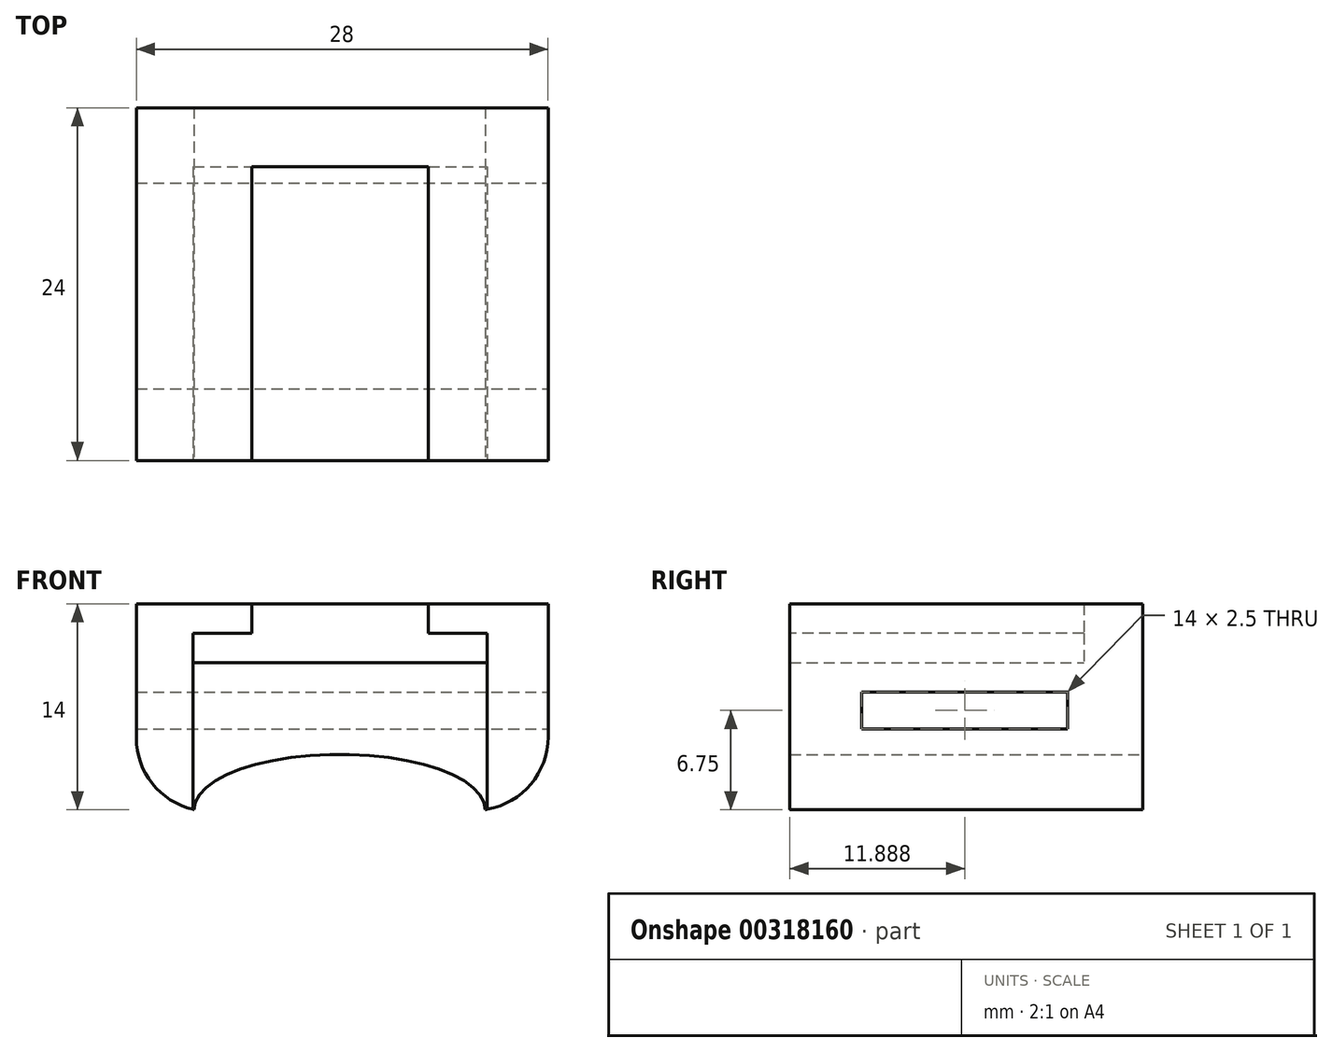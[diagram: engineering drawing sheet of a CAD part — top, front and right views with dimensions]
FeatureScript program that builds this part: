
annotation { "Feature Type Name" : "Feature", "Feature Type Description" : "" }
export const myFeature = defineFeature(function(context is Context, id is Id, definition is map)
    precondition{}
    {
        {
            var Q0;
            Q0=qCreatedBy(makeId("Top.planeOp"),FACE);
            var sketch = newSketch(context, id + "F0", { "sketchPlane" : qUnion([Q0])});
            skLineSegment(sketch, "E0.bottom", {"start": v(-9.96, 9.84) * mm, "end": v(10.04, 9.84) * mm});
            skLineSegment(sketch, "E0.top", {"start": v(-9.96, -10.16) * mm, "end": v(10.04, -10.16) * mm});
            skLineSegment(sketch, "E0.left", {"start": v(-9.96, 9.84) * mm, "end": v(-9.96, -10.16) * mm});
            skLineSegment(sketch, "E0.right", {"start": v(10.04, 9.84) * mm, "end": v(10.04, -10.16) * mm});
            skLineSegment(sketch, "E1.bottom", {"start": v(-13.83, 13.84) * mm, "end": v(14.17, 13.84) * mm});
            skLineSegment(sketch, "E1.top", {"start": v(-13.83, -10.16) * mm, "end": v(14.17, -10.16) * mm});
            skLineSegment(sketch, "E1.left", {"start": v(-13.83, 13.84) * mm, "end": v(-13.83, -10.16) * mm});
            skLineSegment(sketch, "E1.right", {"start": v(14.17, 13.84) * mm, "end": v(14.17, -10.16) * mm});
            skLineSegment(sketch, "E2", {"start": v(-5.96, 9.84) * mm, "end": v(-5.96, -10.16) * mm});
            skLineSegment(sketch, "E3", {"start": v(6.04, 9.84) * mm, "end": v(6.04, -10.16) * mm});
            skLineSegment(sketch, "E4.bottom", {"start": v(-35.1, 18.75) * mm, "end": v(34.9, 18.75) * mm});
            skLineSegment(sketch, "E4.top", {"start": v(-35.1, -15.3) * mm, "end": v(34.9, -15.3) * mm});
            skLineSegment(sketch, "E4.left", {"start": v(-35.1, 18.75) * mm, "end": v(-35.1, -15.3) * mm});
            skLineSegment(sketch, "E4.right", {"start": v(34.9, 18.75) * mm, "end": v(34.9, -15.3) * mm});
            skSolve(sketch);
        }
        {
            var Q0;
            {var subQ0=sQuery(id+"F0.wireOp",EDGE,"E0.left");Q0=makeQuery(id+"F0.imprint","IMPRINT",FACE,{"disambiguationData":[TD([[makeQuery(id+"F0.imprint","IMPRINT",EDGE,{"derivedFrom":subQ0}),1.0]])]});}
            var Q1;
            {var subQ1=sQuery(id+"F0.wireOp",EDGE,"E0.left");Q1=makeQuery(id+"F0.imprint","IMPRINT",FACE,{"disambiguationData":[TD([[makeQuery(id+"F0.imprint","IMPRINT",EDGE,{"derivedFrom":subQ1}),-1.0]])]});}
            var Q2;
            {var subQ0=sQuery(id+"F0.wireOp",EDGE,"E0.right");Q2=makeQuery(id+"F0.imprint","IMPRINT",FACE,{"disambiguationData":[TD([[makeQuery(id+"F0.imprint","IMPRINT",EDGE,{"derivedFrom":subQ0}),-1.0]])]});}
            var Q3;
            {var subQ0=sQuery(id+"F0.wireOp",EDGE,"E2");Q3=makeQuery(id+"F0.imprint","IMPRINT",FACE,{"disambiguationData":[TD([[makeQuery(id+"F0.imprint","IMPRINT",EDGE,{"derivedFrom":subQ0}),1.0]])]});}
            extrude(context, id + "F1", {"entities" : qUnion([Q0, Q1, Q2, Q3]), "depth" : 10 * mm, "offsetDistance" : 25 * mm});
        }
        {
            var Q0;
            {var subQ1=sQuery(id+"F0.wireOp",EDGE,"E0.left");Q0=makeQuery(id+"F0.imprint","IMPRINT",FACE,{"disambiguationData":[TD([[makeQuery(id+"F0.imprint","IMPRINT",EDGE,{"derivedFrom":subQ1}),-1.0]])]});}
            extrude(context, id + "F2", {"entities" : qUnion([Q0]), "operationType" : NewBodyOperationType.ADD, "depth" : 14 * mm, "offsetDistance" : 25 * mm});
        }
        {
            var Q0;
            {var subQ0=sQuery(id+"F0.wireOp",EDGE,"E0.right");var subQ1=sQuery(id+"F0.wireOp",EDGE,"E0.bottom");var subQ2=makeQuery(id+"F0.imprint","INTERSECT",VERTEX,{"derivedFrom":[subQ1,subQ0]});Q0=makeQuery(id+"F0.imprint","IMPRINT",FACE,{"disambiguationData":[TD([[makeQuery(id+"F0.imprint","IMPRINT",EDGE,{"disambiguationData":[TD([[subQ2,1.0]])],"derivedFrom":subQ1}),-1.0]])]});}
            var Q1;
            {var subQ0=sQuery(id+"F0.wireOp",EDGE,"E0.left");var subQ1=sQuery(id+"F0.wireOp",EDGE,"E0.bottom");var subQ2=makeQuery(id+"F0.imprint","INTERSECT",VERTEX,{"derivedFrom":[subQ1,subQ0]});Q1=makeQuery(id+"F0.imprint","IMPRINT",FACE,{"disambiguationData":[TD([[makeQuery(id+"F0.imprint","IMPRINT",EDGE,{"disambiguationData":[TD([[subQ2,-1.0]])],"derivedFrom":subQ1}),-1.0]])]});}
            extrude(context, id + "F3", {"entities" : qUnion([Q0, Q1]), "operationType" : NewBodyOperationType.ADD, "depth" : 14 * mm, "offsetDistance" : 25 * mm, "hasSecondDirection" : true, "secondDirectionOppositeDirection" : false, "secondDirectionDepth" : 12 * mm});
        }
        {
            var Q0;
            Q0=qCreatedBy(makeId("Right.planeOp"),FACE);
            var sketch = newSketch(context, id + "F4", { "sketchPlane" : qUnion([Q0])});
            skLineSegment(sketch, "E5.bottom", {"start": v(8.73, 8) * mm, "end": v(-5.27, 8) * mm});
            skLineSegment(sketch, "E5.top", {"start": v(8.73, 5.5) * mm, "end": v(-5.27, 5.5) * mm});
            skLineSegment(sketch, "E5.left", {"start": v(8.73, 8) * mm, "end": v(8.73, 5.5) * mm});
            skLineSegment(sketch, "E5.right", {"start": v(-5.27, 8) * mm, "end": v(-5.27, 5.5) * mm});
            skSolve(sketch);
        }
        {
            var Q0;
            Q0=makeQuery(id+"F4.imprint","IMPRINT",FACE,{"disambiguationData":[TD([[makeQuery(id+"F4.imprint","IMPRINT",EDGE,{"derivedFrom":sQuery(id+"F4.wireOp",EDGE,"E5.bottom")}),1.0]])]});
            extrude(context, id + "F5", {"entities" : qUnion([Q0]), "operationType" : NewBodyOperationType.REMOVE, "oppositeDirection" : true, "depth" : 25 * mm, "offsetDistance" : 25 * mm, "hasSecondDirection" : true, "secondDirectionOppositeDirection" : false, "secondDirectionDepth" : 25 * mm});
        }
        {
            var Q0;
            Q0=qCreatedBy(makeId("Front.planeOp"),FACE);
            var sketch = newSketch(context, id + "F6", { "sketchPlane" : qUnion([Q0])});
            skEllipse(sketch, "E6", {"center": v(0, 0) * mm, "majorRadius": 9.9 * mm, "minorRadius": 3.76 * mm, "majorAxis": v(1, 0)});
            skSolve(sketch);
        }
        {
            var Q0;
            Q0=makeQuery(id+"F6.imprint","IMPRINT",FACE,{"disambiguationData":[TD([[makeQuery(id+"F6.imprint","IMPRINT",EDGE,{"derivedFrom":sQuery(id+"F6.wireOp",EDGE,"E6")}),1.0]])]});
            extrude(context, id + "F7", {"entities" : qUnion([Q0]), "operationType" : NewBodyOperationType.REMOVE, "oppositeDirection" : true, "depth" : 25 * mm, "offsetDistance" : 25 * mm, "hasSecondDirection" : true, "secondDirectionOppositeDirection" : false, "secondDirectionDepth" : 25 * mm});
        }
        {
            var Q0;
            Q0=makeQuery(id+"F1.opExtrude","CAP_EDGE",EDGE,{"disambiguationData":[OSD([sQuery(id+"F0.wireOp",EDGE,"E1.right")])],"isStart":true});
            var Q1;
            Q1=makeQuery(id+"F1.opExtrude","CAP_EDGE",EDGE,{"disambiguationData":[OSD([sQuery(id+"F0.wireOp",EDGE,"E1.left")])],"isStart":true});
            fillet(context, id + "F8", {"entities" : qUnion([Q0, Q1]), "radius" : 5 * mm, "tangentPropagation" : true, "allowEdgeOverflow" : false});
        }
    });
